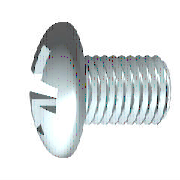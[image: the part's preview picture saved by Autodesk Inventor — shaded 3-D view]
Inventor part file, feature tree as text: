
AUTODESK INVENTOR PART (.ipt)
format: ipt  version: 2020 (Build 240168000, 168)  size: 274,432 bytes
history: native  units: mm (DEFAULTED — no unit token found)
features: other x2, plane x2, extrude x1
ambient origin geometry x7: Origin, YZ Plane, XZ Plane, X Axis, Y Axis, Z Axis, Center Point
bodies: Solid1 (feature_tree)
feature tree (5):
  other  "Базовый элемент"
  plane  "Work Plane1"
  extrude  "Паз"  Depth=3.0mm
  other  "Вырез"
  plane  "Work Plane3"
